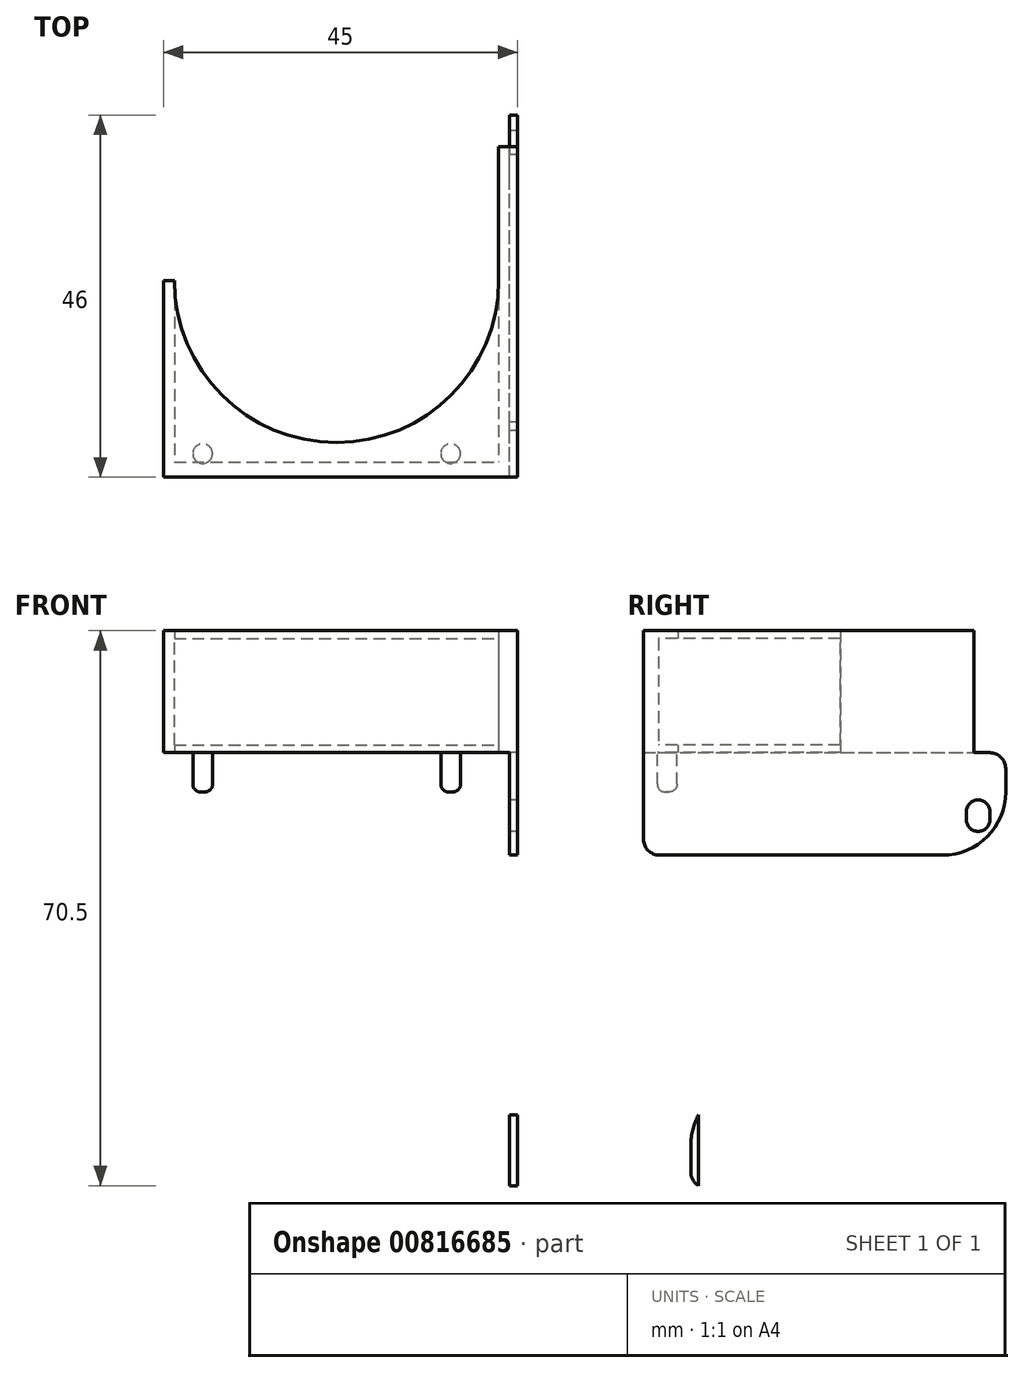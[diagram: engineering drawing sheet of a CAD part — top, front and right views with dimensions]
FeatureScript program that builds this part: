
annotation { "Feature Type Name" : "Feature", "Feature Type Description" : "" }
export const myFeature = defineFeature(function(context is Context, id is Id, definition is map)
    precondition{}
    {
        {
            var Q0;
            Q0=qCreatedBy(makeId("Top.planeOp"),FACE);
            var sketch = newSketch(context, id + "F0", { "sketchPlane" : qUnion([Q0])});
            skLineSegment(sketch, "E0.bottom", {"start": v(22, -21) * mm, "end": v(-22, -21) * mm});
            skLineSegment(sketch, "E0.top", {"start": v(22, 21) * mm, "end": v(-22, 21) * mm});
            skLineSegment(sketch, "E0.left", {"start": v(22, -21) * mm, "end": v(22, 21) * mm});
            skLineSegment(sketch, "E0.right", {"start": v(-22, -21) * mm, "end": v(-22, 21) * mm});
            skPoint(sketch, "E0.middle", {"position": v(0, 0) * mm});
            skSolve(sketch);
        }
        {
            var Q0;
            Q0=makeQuery(id+"F0.imprint","IMPRINT",FACE,{"disambiguationData":[TD([[makeQuery(id+"F0.imprint","IMPRINT",EDGE,{"derivedFrom":sQuery(id+"F0.wireOp",EDGE,"E0.bottom")}),-1.0]])]});
            extrude(context, id + "F1", {"entities" : qUnion([Q0]), "depth" : 1 * mm, "offsetDistance" : 25 * mm});
        }
        {
            var Q0;
            Q0=makeQuery(id+"F1.opExtrude","CAP_FACE",FACE,{"disambiguationData":[OSD([sQuery(id+"F0.wireOp",EDGE,"E0.bottom"),sQuery(id+"F0.wireOp",EDGE,"E0.top"),sQuery(id+"F0.wireOp",EDGE,"E0.left"),sQuery(id+"F0.wireOp",EDGE,"E0.right")])],"isStart":false});
            var sketch = newSketch(context, id + "F2", { "sketchPlane" : qUnion([Q0])});
            skLineSegment(sketch, "E1.bottom", {"start": v(-20.6, 21) * mm, "end": v(20.6, 21) * mm});
            skLineSegment(sketch, "E1.top", {"start": v(-20.6, -19.1) * mm, "end": v(20.6, -19.1) * mm});
            skLineSegment(sketch, "E1.left", {"start": v(-20.6, 21) * mm, "end": v(-20.6, -19.1) * mm});
            skLineSegment(sketch, "E1.right", {"start": v(20.6, 21) * mm, "end": v(20.6, -19.1) * mm});
            skSolve(sketch);
        }
        {
            var Q0;
            Q0=makeQuery(id+"F2.imprint","IMPRINT",FACE,{"disambiguationData":[TD([[makeQuery(id+"F2.imprint","IMPRINT",EDGE,{"derivedFrom":sQuery(id+"F2.wireOp",EDGE,"E1.top")}),-1.0]])]});
            extrude(context, id + "F3", {"entities" : qUnion([Q0]), "operationType" : NewBodyOperationType.ADD, "depth" : 13.5 * mm, "offsetDistance" : 25 * mm});
        }
        {
            var Q0;
            Q0=makeQuery(id+"F3.opExtrude","CAP_FACE",FACE,{"disambiguationData":[OSD([sQuery(id+"F0.wireOp",EDGE,"E0.bottom"),sQuery(id+"F0.wireOp",EDGE,"E0.top"),sQuery(id+"F0.wireOp",EDGE,"E0.left"),sQuery(id+"F0.wireOp",EDGE,"E0.right"),sQuery(id+"F2.wireOp",EDGE,"E1.top"),sQuery(id+"F2.wireOp",EDGE,"E1.left"),sQuery(id+"F2.wireOp",EDGE,"E1.right")])],"isStart":false});
            var sketch = newSketch(context, id + "F4", { "sketchPlane" : qUnion([Q0])});
            skLineSegment(sketch, "E2.bottom", {"start": v(-22, -21) * mm, "end": v(22, -21) * mm});
            skLineSegment(sketch, "E2.top", {"start": v(-22, 21) * mm, "end": v(22, 21) * mm});
            skLineSegment(sketch, "E2.left", {"start": v(-22, -21) * mm, "end": v(-22, 21) * mm});
            skLineSegment(sketch, "E2.right", {"start": v(22, -21) * mm, "end": v(22, 21) * mm});
            skLineSegment(sketch, "E3", {"start": v(0, 21) * mm, "end": v(0, -19.1) * mm, "construction": true});
            skSolve(sketch);
        }
        {
            var Q0;
            Q0=makeQuery(id+"F4.imprint","IMPRINT",FACE,{"disambiguationData":[TD([[makeQuery(id+"F4.imprint","IMPRINT",EDGE,{"derivedFrom":makeQuery(id+"F3.opExtrude","CAP_EDGE",EDGE,{"disambiguationData":[OSD([sQuery(id+"F2.wireOp",EDGE,"E1.top")])],"isStart":false})}),1.0]])]});
            var Q1;
            Q1=makeQuery(id+"F4.imprint","IMPRINT",FACE,{"disambiguationData":[TD([[makeQuery(id+"F4.imprint","IMPRINT",EDGE,{"derivedFrom":sQuery(id+"F4.wireOp",EDGE,"E2.bottom")}),-1.0]])]});
            extrude(context, id + "F5", {"entities" : qUnion([Q0, Q1]), "operationType" : NewBodyOperationType.ADD, "depth" : 1 * mm, "offsetDistance" : 25 * mm});
        }
        {
            var Q0;
            Q0=makeQuery(id+"F1.opExtrude","CAP_FACE",FACE,{"disambiguationData":[OSD([sQuery(id+"F0.wireOp",EDGE,"E0.bottom"),sQuery(id+"F0.wireOp",EDGE,"E0.top"),sQuery(id+"F0.wireOp",EDGE,"E0.left"),sQuery(id+"F0.wireOp",EDGE,"E0.right")])],"isStart":false});
            var sketch = newSketch(context, id + "F6", { "sketchPlane" : qUnion([Q0])});
            skLineSegment(sketch, "E4", {"start": v(0, 21) * mm, "end": v(0, -19.1) * mm, "construction": true});
            skCircle(sketch, "E5", {"center": v(0, 4) * mm, "radius": 20.6 * mm});
            skSolve(sketch);
        }
        {
            var Q0;
            {var subQ0=sQuery(id+"F6.wireOp",EDGE,"E5");var subQ1=makeQuery(id+"F1.opExtrude","CAP_EDGE",EDGE,{"disambiguationData":[OSD([sQuery(id+"F0.wireOp",EDGE,"E0.top")])],"isStart":false});var subQ2=makeQuery(id+"F6.imprint","INTERSECT",VERTEX,{"disambiguationData":[OD(0.0)],"derivedFrom":[subQ1,subQ0]});Q0=makeQuery(id+"F6.imprint","IMPRINT",FACE,{"disambiguationData":[TD([[makeQuery(id+"F6.imprint","IMPRINT",EDGE,{"disambiguationData":[TD([[subQ2,1.0]])],"derivedFrom":subQ0}),1.0]])]});}
            var Q1;
            {var subQ0=sQuery(id+"F6.wireOp",EDGE,"E5");var subQ1=makeQuery(id+"F1.opExtrude","CAP_EDGE",EDGE,{"disambiguationData":[OSD([sQuery(id+"F0.wireOp",EDGE,"E0.top")])],"isStart":false});var subQ2=makeQuery(id+"F6.imprint","INTERSECT",VERTEX,{"disambiguationData":[OD(1.0)],"derivedFrom":[subQ1,subQ0]});Q1=makeQuery(id+"F6.imprint","IMPRINT",FACE,{"disambiguationData":[TD([[makeQuery(id+"F6.imprint","IMPRINT",EDGE,{"disambiguationData":[TD([[subQ2,-1.0]])],"derivedFrom":subQ0}),-1.0]])]});}
            var Q2;
            {var subQ0=sQuery(id+"F6.wireOp",EDGE,"E5");var subQ1=makeQuery(id+"F1.opExtrude","CAP_EDGE",EDGE,{"disambiguationData":[OSD([sQuery(id+"F0.wireOp",EDGE,"E0.top")])],"isStart":false});var subQ2=makeQuery(id+"F6.imprint","INTERSECT",VERTEX,{"disambiguationData":[OD(0.0)],"derivedFrom":[subQ1,subQ0]});Q2=makeQuery(id+"F6.imprint","IMPRINT",FACE,{"disambiguationData":[TD([[makeQuery(id+"F6.imprint","IMPRINT",EDGE,{"disambiguationData":[TD([[subQ2,1.0]])],"derivedFrom":subQ0}),-1.0]])]});}
            extrude(context, id + "F7", {"entities" : qUnion([Q0, Q1, Q2]), "operationType" : NewBodyOperationType.REMOVE, "endBound" : BoundingType.SYMMETRIC, "depth" : 50 * mm, "offsetDistance" : 25 * mm});
        }
        {
            var Q0;
            Q0=makeQuery(id+"F1.opExtrude","CAP_FACE",FACE,{"disambiguationData":[OSD([sQuery(id+"F0.wireOp",EDGE,"E0.bottom"),sQuery(id+"F0.wireOp",EDGE,"E0.top"),sQuery(id+"F0.wireOp",EDGE,"E0.left"),sQuery(id+"F0.wireOp",EDGE,"E0.right")])],"isStart":true});
            var sketch = newSketch(context, id + "F8", { "sketchPlane" : qUnion([Q0])});
            skPoint(sketch, "E6", {"position": v(-17, 18) * mm});
            skPoint(sketch, "E7", {"position": v(14.5, 18) * mm});
            skCircle(sketch, "E8", {"center": v(-17, 18) * mm, "radius": 1.25 * mm});
            skCircle(sketch, "E9", {"center": v(14.5, 18) * mm, "radius": 1.25 * mm});
            skSolve(sketch);
        }
        {
            var Q0;
            Q0=makeQuery(id+"F4.imprint","IMPRINT",FACE,{"disambiguationData":[TD([[makeQuery(id+"F4.imprint","IMPRINT",EDGE,{"derivedFrom":sQuery(id+"F4.wireOp",EDGE,"E2.bottom")}),-1.0]])]});
            var Q1;
            {var subQ0=sQuery(id+"F4.wireOp",EDGE,"bKkrmM3L-GTnI-I3aD-yFF0-BNDNTabTKxPm");var subQ1=makeQuery(id+"F3.opExtrude","CAP_EDGE",EDGE,{"disambiguationData":[OSD([sQuery(id+"F2.wireOp",EDGE,"E1.left")])],"isStart":false});var subQ2=makeQuery(id+"F4.imprint","INTERSECT",VERTEX,{"derivedFrom":[subQ1,subQ0]});Q1=makeQuery(id+"F4.imprint","IMPRINT",FACE,{"disambiguationData":[TD([[makeQuery(id+"F4.imprint","IMPRINT",EDGE,{"disambiguationData":[TD([[subQ2,-1.0]])],"derivedFrom":subQ0}),-1.0]])]});}
            var Q2;
            {var subQ0=sQuery(id+"F4.wireOp",EDGE,"bKkrmM3L-GTnI-I3aD-yFF0-BNDNTabTKxPm");var subQ1=makeQuery(id+"F3.opExtrude","CAP_EDGE",EDGE,{"disambiguationData":[OSD([sQuery(id+"F2.wireOp",EDGE,"E1.right")])],"isStart":false});var subQ2=makeQuery(id+"F4.imprint","INTERSECT",VERTEX,{"derivedFrom":[subQ1,subQ0]});Q2=makeQuery(id+"F4.imprint","IMPRINT",FACE,{"disambiguationData":[TD([[makeQuery(id+"F4.imprint","IMPRINT",EDGE,{"disambiguationData":[TD([[subQ2,1.0]])],"derivedFrom":subQ0}),-1.0]])]});}
            extrude(context, id + "F9", {"entities" : qUnion([Q0, Q1, Q2]), "operationType" : NewBodyOperationType.ADD, "depth" : 1 * mm, "offsetDistance" : 25 * mm});
        }
        {
            var Q0;
            {var subQ0=sQuery(id+"F2.wireOp",EDGE,"E1.left");Q0=makeQuery(id+"F9.boolean.opBoolean","MERGE",FACE,{"derivedFrom":[makeQuery(id+"F7.boolean.opBoolean","MERGE",FACE,{"derivedFrom":[makeQuery(id+"F3.opExtrude","SWEPT_FACE",FACE,{"disambiguationData":[OSD([subQ0])]}),makeQuery(id+"F7.opExtrude","SWEPT_FACE",FACE,{"disambiguationData":[OSD([subQ0])]})]}),makeQuery(id+"F9.opExtrude","SWEPT_FACE",FACE,{"disambiguationData":[OSD([subQ0])]})]});}
            var sketch = newSketch(context, id + "F10", { "sketchPlane" : qUnion([Q0])});
            skLineSegment(sketch, "E10.bottom", {"start": v(21, 15) * mm, "end": v(21, 15) * mm});
            skLineSegment(sketch, "E10.top", {"start": v(21, 0) * mm, "end": v(21, 0) * mm});
            skLineSegment(sketch, "E10.left", {"start": v(21, 15) * mm, "end": v(21, 0) * mm});
            skLineSegment(sketch, "E10.right", {"start": v(21, 15) * mm, "end": v(21, 0) * mm});
            skLineSegment(sketch, "E11.bottom", {"start": v(21, 0) * mm, "end": v(4, 0) * mm});
            skLineSegment(sketch, "E11.top", {"start": v(21, 15.5) * mm, "end": v(4, 15.5) * mm});
            skLineSegment(sketch, "E11.left", {"start": v(21, 0) * mm, "end": v(21, 15.5) * mm});
            skLineSegment(sketch, "E11.right", {"start": v(4, 0) * mm, "end": v(4, 15.5) * mm});
            skSolve(sketch);
        }
        {
            var Q0;
            {var subQ4=sQuery(id+"F10.wireOp",EDGE,"E11.bottom");Q0=makeQuery(id+"F10.imprint","IMPRINT",FACE,{"disambiguationData":[TD([[makeQuery(id+"F10.imprint","IMPRINT",EDGE,{"derivedFrom":subQ4}),1.0]])]});}
            extrude(context, id + "F11", {"entities" : qUnion([Q0]), "operationType" : NewBodyOperationType.REMOVE, "oppositeDirection" : true, "depth" : 25 * mm, "offsetDistance" : 25 * mm});
        }
        {
            var Q0;
            {var subQ0=sQuery(id+"F0.wireOp",EDGE,"E0.left");Q0=makeQuery(id+"F9.boolean.opBoolean","MERGE",FACE,{"derivedFrom":[makeQuery(id+"F3.boolean.opBoolean","MERGE",FACE,{"derivedFrom":[makeQuery(id+"F1.opExtrude","SWEPT_FACE",FACE,{"disambiguationData":[OSD([subQ0])]}),makeQuery(id+"F3.opExtrude","SWEPT_FACE",FACE,{"disambiguationData":[OSD([subQ0])]})]}),makeQuery(id+"F9.opExtrude","SWEPT_FACE",FACE,{"disambiguationData":[OSD([sQuery(id+"F4.wireOp",EDGE,"E2.right")])]})]});}
            var sketch = newSketch(context, id + "F12", { "sketchPlane" : qUnion([Q0])});
            skLineSegment(sketch, "E12.bottom", {"start": v(-21, 15.5) * mm, "end": v(21, 15.5) * mm});
            skLineSegment(sketch, "E12.top", {"start": v(-21, 0) * mm, "end": v(21, 0) * mm});
            skLineSegment(sketch, "E12.left", {"start": v(-21, 15.5) * mm, "end": v(-21, 0) * mm});
            skLineSegment(sketch, "E12.right", {"start": v(21, 15.5) * mm, "end": v(21, 0) * mm});
            skLineSegment(sketch, "E13.bottom", {"start": v(-21, 0) * mm, "end": v(25, 0) * mm});
            skLineSegment(sketch, "E13.top", {"start": v(-21, -13) * mm, "end": v(25, -13) * mm});
            skLineSegment(sketch, "E13.left", {"start": v(-21, 0) * mm, "end": v(-21, -13) * mm});
            skLineSegment(sketch, "E13.right", {"start": v(25, 0) * mm, "end": v(25, -13) * mm});
            skPoint(sketch, "E14", {"position": v(21.5, -8) * mm});
            skPoint(sketch, "E15", {"position": v(-18, -10) * mm});
            skLineSegment(sketch, "E16.bottom", {"start": v(-21, -13) * mm, "end": v(-15, -13) * mm});
            skLineSegment(sketch, "E16.top", {"start": v(-21, -55) * mm, "end": v(-15, -55) * mm});
            skLineSegment(sketch, "E16.left", {"start": v(-21, -13) * mm, "end": v(-21, -55) * mm});
            skLineSegment(sketch, "E16.right", {"start": v(-15, -13) * mm, "end": v(-15, -55) * mm});
            skPoint(sketch, "E17", {"position": v(-18, -50) * mm});
            skLineSegment(sketch, "E18", {"start": v(-18, -10) * mm, "end": v(-18, -55) * mm, "construction": true});
            skLineSegment(sketch, "E19.bottom", {"start": v(23, -8.5) * mm, "end": v(20, -8.5) * mm});
            skLineSegment(sketch, "E19.top", {"start": v(23, -7.5) * mm, "end": v(20, -7.5) * mm});
            skLineSegment(sketch, "E19.left", {"start": v(23, -8.5) * mm, "end": v(23, -7.5) * mm});
            skLineSegment(sketch, "E19.right", {"start": v(20, -8.5) * mm, "end": v(20, -7.5) * mm});
            skCircle(sketch, "E20", {"center": v(21.5, -7.5) * mm, "radius": 1.5 * mm});
            skCircle(sketch, "E21", {"center": v(21.5, -8.5) * mm, "radius": 1.5 * mm});
            skLineSegment(sketch, "E22.bottom", {"start": v(-16.45, -50.5) * mm, "end": v(-19.55, -50.5) * mm});
            skLineSegment(sketch, "E22.top", {"start": v(-16.45, -49.5) * mm, "end": v(-19.55, -49.5) * mm});
            skLineSegment(sketch, "E22.left", {"start": v(-16.45, -50.5) * mm, "end": v(-16.45, -49.5) * mm});
            skLineSegment(sketch, "E22.right", {"start": v(-19.55, -50.5) * mm, "end": v(-19.55, -49.5) * mm});
            skCircle(sketch, "E23", {"center": v(-18, -49.5) * mm, "radius": 1.55 * mm});
            skCircle(sketch, "E24", {"center": v(-18, -50.5) * mm, "radius": 1.55 * mm});
            skLineSegment(sketch, "E25.bottom", {"start": v(-15, -55) * mm, "end": v(-14, -55) * mm});
            skLineSegment(sketch, "E25.top", {"start": v(-15, -46) * mm, "end": v(-14, -46) * mm});
            skLineSegment(sketch, "E25.left", {"start": v(-15, -55) * mm, "end": v(-15, -46) * mm});
            skLineSegment(sketch, "E25.right", {"start": v(-14, -55) * mm, "end": v(-14, -46) * mm});
            skSolve(sketch);
        }
        {
            var Q0;
            Q0=makeQuery(id+"F12.imprint","IMPRINT",FACE,{"disambiguationData":[TD([[makeQuery(id+"F12.imprint","IMPRINT",EDGE,{"derivedFrom":sQuery(id+"F12.wireOp",EDGE,"E13.top")}),1.0]])]});
            var Q1;
            Q1=makeQuery(id+"F12.imprint","IMPRINT",FACE,{"disambiguationData":[TD([[makeQuery(id+"F12.imprint","IMPRINT",EDGE,{"derivedFrom":sQuery(id+"F12.wireOp",EDGE,"E16.bottom")}),-1.0]])]});
            var Q2;
            Q2=makeQuery(id+"F12.imprint","IMPRINT",FACE,{"disambiguationData":[TD([[makeQuery(id+"F12.imprint","IMPRINT",EDGE,{"derivedFrom":sQuery(id+"F12.wireOp",EDGE,"E12.bottom")}),-1.0]])]});
            var Q3;
            Q3=makeQuery(id+"F12.imprint","IMPRINT",FACE,{"disambiguationData":[TD([[makeQuery(id+"F12.imprint","IMPRINT",EDGE,{"derivedFrom":sQuery(id+"F12.wireOp",EDGE,"E25.bottom")}),1.0]])]});
            extrude(context, id + "F13", {"entities" : qUnion([Q0, Q1, Q2, Q3]), "operationType" : NewBodyOperationType.ADD, "depth" : 1 * mm, "offsetDistance" : 25 * mm});
        }
        {
            var Q0;
            {var subQ1=sQuery(id+"F12.wireOp",EDGE,"E22.bottom");var subQ3=sQuery(id+"F12.wireOp",EDGE,"E23");var subQ4=makeQuery(id+"F12.imprint","INTERSECT",VERTEX,{"disambiguationData":[OD(0.0)],"derivedFrom":[subQ1,subQ3]});Q0=makeQuery(id+"F12.imprint","IMPRINT",FACE,{"disambiguationData":[TD([[makeQuery(id+"F12.imprint","IMPRINT",EDGE,{"disambiguationData":[TD([[subQ4,1.0]])],"derivedFrom":subQ3}),-1.0]])]});}
            var Q1;
            {var subQ1=sQuery(id+"F12.wireOp",EDGE,"E22.bottom");var subQ3=sQuery(id+"F12.wireOp",EDGE,"E23");var subQ4=makeQuery(id+"F12.imprint","INTERSECT",VERTEX,{"disambiguationData":[OD(0.0)],"derivedFrom":[subQ1,subQ3]});Q1=makeQuery(id+"F12.imprint","IMPRINT",FACE,{"disambiguationData":[TD([[makeQuery(id+"F12.imprint","IMPRINT",EDGE,{"disambiguationData":[TD([[subQ4,-1.0]])],"derivedFrom":subQ3}),-1.0]])]});}
            var Q2;
            {var subQ0=sQuery(id+"F12.wireOp",EDGE,"E22.left");Q2=makeQuery(id+"F12.imprint","IMPRINT",FACE,{"disambiguationData":[TD([[makeQuery(id+"F12.imprint","IMPRINT",EDGE,{"derivedFrom":subQ0}),1.0]])]});}
            var Q3;
            {var subQ1=sQuery(id+"F12.wireOp",EDGE,"E22.top");var subQ3=sQuery(id+"F12.wireOp",EDGE,"E24");var subQ4=makeQuery(id+"F12.imprint","INTERSECT",VERTEX,{"disambiguationData":[OD(0.0)],"derivedFrom":[subQ1,subQ3]});Q3=makeQuery(id+"F12.imprint","IMPRINT",FACE,{"disambiguationData":[TD([[makeQuery(id+"F12.imprint","IMPRINT",EDGE,{"disambiguationData":[TD([[subQ4,1.0]])],"derivedFrom":subQ3}),-1.0]])]});}
            var Q4;
            {var subQ1=sQuery(id+"F12.wireOp",EDGE,"E22.top");var subQ3=sQuery(id+"F12.wireOp",EDGE,"E24");var subQ4=makeQuery(id+"F12.imprint","INTERSECT",VERTEX,{"disambiguationData":[OD(0.0)],"derivedFrom":[subQ1,subQ3]});Q4=makeQuery(id+"F12.imprint","IMPRINT",FACE,{"disambiguationData":[TD([[makeQuery(id+"F12.imprint","IMPRINT",EDGE,{"disambiguationData":[TD([[subQ4,-1.0]])],"derivedFrom":subQ3}),-1.0]])]});}
            var Q5;
            {var subQ0=sQuery(id+"F12.wireOp",EDGE,"E24");var subQ1=sQuery(id+"F12.wireOp",EDGE,"E22.top");var subQ2=makeQuery(id+"F12.imprint","INTERSECT",VERTEX,{"disambiguationData":[OD(0.0)],"derivedFrom":[subQ1,subQ0]});Q5=makeQuery(id+"F12.imprint","IMPRINT",FACE,{"disambiguationData":[TD([[makeQuery(id+"F12.imprint","IMPRINT",EDGE,{"disambiguationData":[TD([[subQ2,-1.0]])],"derivedFrom":subQ1}),-1.0]])]});}
            var Q6;
            {var subQ0=sQuery(id+"F12.wireOp",EDGE,"E23");var subQ1=sQuery(id+"F12.wireOp",EDGE,"E22.bottom");var subQ2=makeQuery(id+"F12.imprint","INTERSECT",VERTEX,{"disambiguationData":[OD(0.0)],"derivedFrom":[subQ1,subQ0]});Q6=makeQuery(id+"F12.imprint","IMPRINT",FACE,{"disambiguationData":[TD([[makeQuery(id+"F12.imprint","IMPRINT",EDGE,{"disambiguationData":[TD([[subQ2,-1.0]])],"derivedFrom":subQ1}),-1.0]])]});}
            var Q7;
            {var subQ0=sQuery(id+"F12.wireOp",EDGE,"E23");var subQ1=sQuery(id+"F12.wireOp",EDGE,"E22.bottom");var subQ2=makeQuery(id+"F12.imprint","INTERSECT",VERTEX,{"disambiguationData":[OD(0.0)],"derivedFrom":[subQ1,subQ0]});Q7=makeQuery(id+"F12.imprint","IMPRINT",FACE,{"disambiguationData":[TD([[makeQuery(id+"F12.imprint","IMPRINT",EDGE,{"disambiguationData":[TD([[subQ2,-1.0]])],"derivedFrom":subQ1}),1.0]])]});}
            var Q8;
            {var subQ1=sQuery(id+"F12.wireOp",EDGE,"E22.bottom");var subQ3=sQuery(id+"F12.wireOp",EDGE,"E23");var subQ4=makeQuery(id+"F12.imprint","INTERSECT",VERTEX,{"disambiguationData":[OD(1.0)],"derivedFrom":[subQ1,subQ3]});Q8=makeQuery(id+"F12.imprint","IMPRINT",FACE,{"disambiguationData":[TD([[makeQuery(id+"F12.imprint","IMPRINT",EDGE,{"disambiguationData":[TD([[subQ4,1.0]])],"derivedFrom":subQ3}),-1.0]])]});}
            var Q9;
            {var subQ0=sQuery(id+"F12.wireOp",EDGE,"E22.right");Q9=makeQuery(id+"F12.imprint","IMPRINT",FACE,{"disambiguationData":[TD([[makeQuery(id+"F12.imprint","IMPRINT",EDGE,{"derivedFrom":subQ0}),-1.0]])]});}
            var Q10;
            {var subQ1=sQuery(id+"F12.wireOp",EDGE,"E22.top");var subQ3=sQuery(id+"F12.wireOp",EDGE,"E24");var subQ4=makeQuery(id+"F12.imprint","INTERSECT",VERTEX,{"disambiguationData":[OD(1.0)],"derivedFrom":[subQ1,subQ3]});Q10=makeQuery(id+"F12.imprint","IMPRINT",FACE,{"disambiguationData":[TD([[makeQuery(id+"F12.imprint","IMPRINT",EDGE,{"disambiguationData":[TD([[subQ4,-1.0]])],"derivedFrom":subQ3}),-1.0]])]});}
            var Q11;
            {var subQ1=sQuery(id+"F12.wireOp",EDGE,"E19.bottom");var subQ3=sQuery(id+"F12.wireOp",EDGE,"E20");var subQ4=makeQuery(id+"F12.imprint","INTERSECT",VERTEX,{"disambiguationData":[OD(0.0)],"derivedFrom":[subQ1,subQ3]});Q11=makeQuery(id+"F12.imprint","IMPRINT",FACE,{"disambiguationData":[TD([[makeQuery(id+"F12.imprint","IMPRINT",EDGE,{"disambiguationData":[TD([[subQ4,1.0]])],"derivedFrom":subQ3}),-1.0]])]});}
            var Q12;
            {var subQ1=sQuery(id+"F12.wireOp",EDGE,"E19.bottom");var subQ3=sQuery(id+"F12.wireOp",EDGE,"E20");var subQ4=makeQuery(id+"F12.imprint","INTERSECT",VERTEX,{"disambiguationData":[OD(1.0)],"derivedFrom":[subQ1,subQ3]});Q12=makeQuery(id+"F12.imprint","IMPRINT",FACE,{"disambiguationData":[TD([[makeQuery(id+"F12.imprint","IMPRINT",EDGE,{"disambiguationData":[TD([[subQ4,1.0]])],"derivedFrom":subQ3}),-1.0]])]});}
            var Q13;
            {var subQ1=sQuery(id+"F12.wireOp",EDGE,"E19.top");var subQ3=sQuery(id+"F12.wireOp",EDGE,"E21");var subQ4=makeQuery(id+"F12.imprint","INTERSECT",VERTEX,{"disambiguationData":[OD(1.0)],"derivedFrom":[subQ1,subQ3]});Q13=makeQuery(id+"F12.imprint","IMPRINT",FACE,{"disambiguationData":[TD([[makeQuery(id+"F12.imprint","IMPRINT",EDGE,{"disambiguationData":[TD([[subQ4,-1.0]])],"derivedFrom":subQ3}),-1.0]])]});}
            var Q14;
            {var subQ1=sQuery(id+"F12.wireOp",EDGE,"E19.top");var subQ3=sQuery(id+"F12.wireOp",EDGE,"E21");var subQ4=makeQuery(id+"F12.imprint","INTERSECT",VERTEX,{"disambiguationData":[OD(0.0)],"derivedFrom":[subQ1,subQ3]});Q14=makeQuery(id+"F12.imprint","IMPRINT",FACE,{"disambiguationData":[TD([[makeQuery(id+"F12.imprint","IMPRINT",EDGE,{"disambiguationData":[TD([[subQ4,-1.0]])],"derivedFrom":subQ3}),-1.0]])]});}
            var Q15;
            {var subQ0=sQuery(id+"F12.wireOp",EDGE,"E21");var subQ1=sQuery(id+"F12.wireOp",EDGE,"E19.top");var subQ2=makeQuery(id+"F12.imprint","INTERSECT",VERTEX,{"disambiguationData":[OD(0.0)],"derivedFrom":[subQ1,subQ0]});Q15=makeQuery(id+"F12.imprint","IMPRINT",FACE,{"disambiguationData":[TD([[makeQuery(id+"F12.imprint","IMPRINT",EDGE,{"disambiguationData":[TD([[subQ2,-1.0]])],"derivedFrom":subQ1}),-1.0]])]});}
            var Q16;
            {var subQ0=sQuery(id+"F12.wireOp",EDGE,"E20");var subQ1=sQuery(id+"F12.wireOp",EDGE,"E19.bottom");var subQ2=makeQuery(id+"F12.imprint","INTERSECT",VERTEX,{"disambiguationData":[OD(0.0)],"derivedFrom":[subQ1,subQ0]});Q16=makeQuery(id+"F12.imprint","IMPRINT",FACE,{"disambiguationData":[TD([[makeQuery(id+"F12.imprint","IMPRINT",EDGE,{"disambiguationData":[TD([[subQ2,-1.0]])],"derivedFrom":subQ1}),-1.0]])]});}
            var Q17;
            {var subQ0=sQuery(id+"F12.wireOp",EDGE,"E20");var subQ1=sQuery(id+"F12.wireOp",EDGE,"E19.bottom");var subQ2=makeQuery(id+"F12.imprint","INTERSECT",VERTEX,{"disambiguationData":[OD(0.0)],"derivedFrom":[subQ1,subQ0]});Q17=makeQuery(id+"F12.imprint","IMPRINT",FACE,{"disambiguationData":[TD([[makeQuery(id+"F12.imprint","IMPRINT",EDGE,{"disambiguationData":[TD([[subQ2,-1.0]])],"derivedFrom":subQ1}),1.0]])]});}
            var Q18;
            {var subQ0=sQuery(id+"F12.wireOp",EDGE,"E19.left");Q18=makeQuery(id+"F12.imprint","IMPRINT",FACE,{"disambiguationData":[TD([[makeQuery(id+"F12.imprint","IMPRINT",EDGE,{"derivedFrom":subQ0}),1.0]])]});}
            var Q19;
            {var subQ1=sQuery(id+"F12.wireOp",EDGE,"E19.top");var subQ3=sQuery(id+"F12.wireOp",EDGE,"E21");var subQ4=makeQuery(id+"F12.imprint","INTERSECT",VERTEX,{"disambiguationData":[OD(0.0)],"derivedFrom":[subQ1,subQ3]});Q19=makeQuery(id+"F12.imprint","IMPRINT",FACE,{"disambiguationData":[TD([[makeQuery(id+"F12.imprint","IMPRINT",EDGE,{"disambiguationData":[TD([[subQ4,1.0]])],"derivedFrom":subQ3}),-1.0]])]});}
            var Q20;
            {var subQ1=sQuery(id+"F12.wireOp",EDGE,"E19.bottom");var subQ3=sQuery(id+"F12.wireOp",EDGE,"E20");var subQ4=makeQuery(id+"F12.imprint","INTERSECT",VERTEX,{"disambiguationData":[OD(0.0)],"derivedFrom":[subQ1,subQ3]});Q20=makeQuery(id+"F12.imprint","IMPRINT",FACE,{"disambiguationData":[TD([[makeQuery(id+"F12.imprint","IMPRINT",EDGE,{"disambiguationData":[TD([[subQ4,-1.0]])],"derivedFrom":subQ3}),-1.0]])]});}
            var Q21;
            {var subQ0=sQuery(id+"F12.wireOp",EDGE,"E19.right");Q21=makeQuery(id+"F12.imprint","IMPRINT",FACE,{"disambiguationData":[TD([[makeQuery(id+"F12.imprint","IMPRINT",EDGE,{"derivedFrom":subQ0}),-1.0]])]});}
            extrude(context, id + "F14", {"entities" : qUnion([Q0, Q1, Q2, Q3, Q4, Q5, Q6, Q7, Q8, Q9, Q10, Q11, Q12, Q13, Q14, Q15, Q16, Q17, Q18, Q19, Q20, Q21]), "operationType" : NewBodyOperationType.REMOVE, "oppositeDirection" : true, "depth" : 25 * mm, "offsetDistance" : 25 * mm});
        }
        {
            var Q0;
            Q0=makeQuery(id+"F13.opExtrude","SWEPT_EDGE",EDGE,{"disambiguationData":[OSD([sQuery(id+"F12.wireOp",EDGE,"E13.top"),sQuery(id+"F12.wireOp",EDGE,"E16.bottom"),sQuery(id+"F12.wireOp",EDGE,"E16.right")])]});
            fillet(context, id + "F15", {"entities" : qUnion([Q0]), "radius" : 8 * mm, "tangentPropagation" : true, "allowEdgeOverflow" : false});
        }
        {
            var Q0;
            Q0=makeQuery(id+"F13.opExtrude","SWEPT_EDGE",EDGE,{"disambiguationData":[OSD([sQuery(id+"F12.wireOp",EDGE,"E13.bottom"),sQuery(id+"F12.wireOp",EDGE,"E13.right")])]});
            var Q1;
            Q1=makeQuery(id+"F13.opExtrude","SWEPT_EDGE",EDGE,{"disambiguationData":[OSD([sQuery(id+"F12.wireOp",EDGE,"E13.top"),sQuery(id+"F12.wireOp",EDGE,"E13.right")])]});
            var Q2;
            Q2=makeQuery(id+"F13.opExtrude","SWEPT_EDGE",EDGE,{"disambiguationData":[OSD([sQuery(id+"F12.wireOp",EDGE,"E16.top"),sQuery(id+"F12.wireOp",EDGE,"E16.right")])]});
            var Q3;
            Q3=makeQuery(id+"F13.opExtrude","SWEPT_EDGE",EDGE,{"disambiguationData":[OSD([sQuery(id+"F12.wireOp",EDGE,"E16.top"),sQuery(id+"F12.wireOp",EDGE,"E16.left")])]});
            var Q4;
            Q4=makeQuery(id+"F13.opExtrude","SWEPT_EDGE",EDGE,{"disambiguationData":[OSD([sQuery(id+"F12.wireOp",EDGE,"E16.top"),sQuery(id+"F12.wireOp",EDGE,"E25.bottom"),sQuery(id+"F12.wireOp",EDGE,"E25.left")])]});
            var Q5;
            Q5=makeQuery(id+"F13.opExtrude","SWEPT_EDGE",EDGE,{"disambiguationData":[OSD([sQuery(id+"F12.wireOp",EDGE,"E16.right"),sQuery(id+"F12.wireOp",EDGE,"E25.top"),sQuery(id+"F12.wireOp",EDGE,"E25.left")])]});
            fillet(context, id + "F16", {"entities" : qUnion([Q0, Q1, Q2, Q3, Q4, Q5]), "radius" : 2 * mm, "tangentPropagation" : true, "allowEdgeOverflow" : false});
        }
        {
            var Q0;
            Q0=makeQuery(id+"F8.imprint","IMPRINT",FACE,{"disambiguationData":[TD([[makeQuery(id+"F8.imprint","IMPRINT",EDGE,{"derivedFrom":sQuery(id+"F8.wireOp",EDGE,"E8")}),1.0]])]});
            var Q1;
            Q1=makeQuery(id+"F8.imprint","IMPRINT",FACE,{"disambiguationData":[TD([[makeQuery(id+"F8.imprint","IMPRINT",EDGE,{"derivedFrom":sQuery(id+"F8.wireOp",EDGE,"E9")}),1.0]])]});
            extrude(context, id + "F17", {"entities" : qUnion([Q0, Q1]), "operationType" : NewBodyOperationType.ADD, "depth" : 5 * mm, "offsetDistance" : 25 * mm});
        }
        {
            var Q0;
            Q0=makeQuery(id+"F17.opExtrude","CAP_EDGE",EDGE,{"disambiguationData":[OSD([sQuery(id+"F8.wireOp",EDGE,"E8")])],"isStart":false});
            var Q1;
            Q1=makeQuery(id+"F17.opExtrude","CAP_EDGE",EDGE,{"disambiguationData":[OSD([sQuery(id+"F8.wireOp",EDGE,"E9")])],"isStart":false});
            var Q2;
            Q2=makeQuery(id+"F16.opFillet","BLEND_EDGE",EDGE,{"blendedFrom":[makeQuery(id+"F13.opExtrude","SWEPT_EDGE",EDGE,{"disambiguationData":[OSD([sQuery(id+"F12.wireOp",EDGE,"E16.right"),sQuery(id+"F12.wireOp",EDGE,"E25.top"),sQuery(id+"F12.wireOp",EDGE,"E25.left")])]}),makeQuery(id+"F13.opExtrude","SWEPT_FACE",FACE,{"disambiguationData":[OSD([sQuery(id+"F12.wireOp",EDGE,"E25.right")])]})],"blendedInto":[makeQuery(id+"F13.opExtrude","SWEPT_FACE",FACE,{"disambiguationData":[OSD([sQuery(id+"F12.wireOp",EDGE,"E25.right")])]})]});
            fillet(context, id + "F18", {"entities" : qUnion([Q0, Q1, Q2]), "radius" : 1 * mm, "tangentPropagation" : true, "allowEdgeOverflow" : false});
        }
    });
